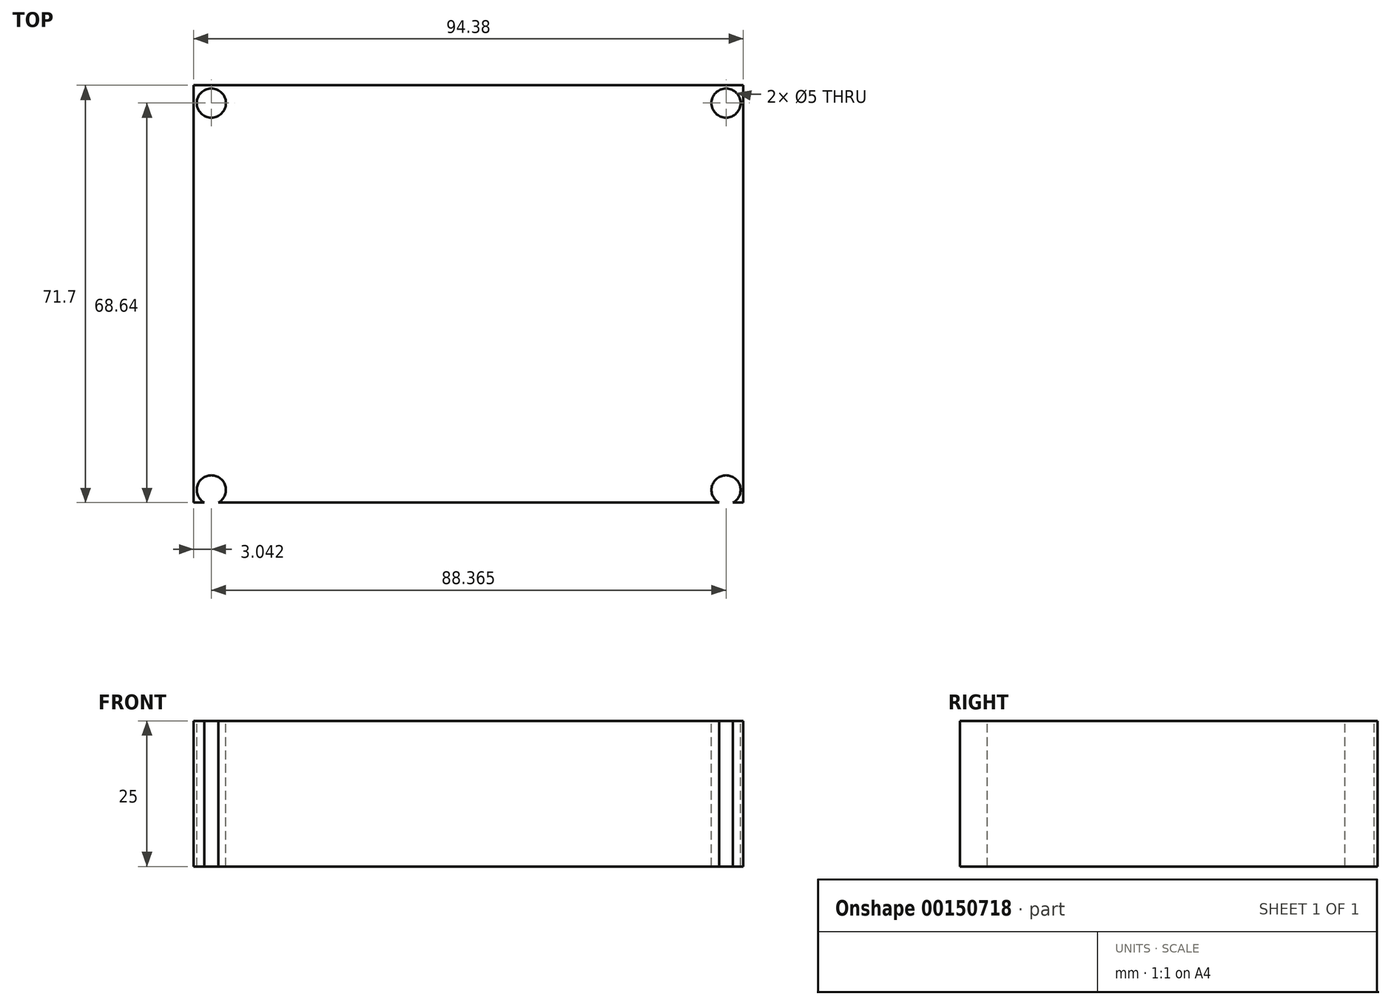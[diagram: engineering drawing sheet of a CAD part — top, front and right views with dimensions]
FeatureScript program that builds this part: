
annotation { "Feature Type Name" : "Feature", "Feature Type Description" : "" }
export const myFeature = defineFeature(function(context is Context, id is Id, definition is map)
    precondition{}
    {
        {
            var Q0;
            Q0=qCreatedBy(makeId("Top.planeOp"),FACE);
            var sketch = newSketch(context, id + "F0", { "sketchPlane" : qUnion([Q0])});
            skLineSegment(sketch, "E0.bottom", {"start": v(47.2, -35.85) * mm, "end": v(-47.2, -35.85) * mm});
            skLineSegment(sketch, "E0.top", {"start": v(47.2, 35.85) * mm, "end": v(-47.2, 35.85) * mm});
            skLineSegment(sketch, "E0.left", {"start": v(47.2, -35.85) * mm, "end": v(47.2, 35.85) * mm});
            skLineSegment(sketch, "E0.right", {"start": v(-47.2, -35.85) * mm, "end": v(-47.2, 35.85) * mm});
            skPoint(sketch, "E0.middle", {"position": v(0, 0) * mm});
            skSolve(sketch);
        }
        {
            var Q0;
            Q0=makeQuery(id+"F0.imprint","IMPRINT",FACE,{"disambiguationData":[TD([[makeQuery(id+"F0.imprint","IMPRINT",EDGE,{"derivedFrom":sQuery(id+"F0.wireOp",EDGE,"E0.bottom")}),-1.0]])]});
            extrude(context, id + "F1", {"entities" : qUnion([Q0]), "depth" : 25 * mm});
        }
        {
            var Q0;
            Q0=makeQuery(id+"F1.opExtrude","CAP_FACE",FACE,{"disambiguationData":[OSD([sQuery(id+"F0.wireOp",EDGE,"E0.bottom"),sQuery(id+"F0.wireOp",EDGE,"E0.top"),sQuery(id+"F0.wireOp",EDGE,"E0.left"),sQuery(id+"F0.wireOp",EDGE,"E0.right")])],"isStart":false});
            var sketch = newSketch(context, id + "F2", { "sketchPlane" : qUnion([Q0])});
            skPoint(sketch, "E1", {"position": v(-44.15, 32.8) * mm});
            skPoint(sketch, "E2", {"position": v(-44.15, -33.66) * mm});
            skPoint(sketch, "E3", {"position": v(44.22, -33.66) * mm});
            skPoint(sketch, "E4", {"position": v(44.22, 32.8) * mm});
            skSolve(sketch);
        }
        {
            var Q0;
            Q0=sQuery(id+"F2.wireOp",VERTEX,"E1");
            var Q1;
            Q1=sQuery(id+"F2.wireOp",VERTEX,"E2");
            var Q2;
            Q2=sQuery(id+"F2.wireOp",VERTEX,"E4");
            var Q3;
            Q3=sQuery(id+"F2.wireOp",VERTEX,"E3");
            var Q4;
            Q4=makeQuery(id+"F1.opExtrude","SWEPT_BODY",BODY,{"disambiguationData":[OSD([sQuery(id+"F0.wireOp",EDGE,"E0.bottom"),sQuery(id+"F0.wireOp",EDGE,"E0.top"),sQuery(id+"F0.wireOp",EDGE,"E0.left"),sQuery(id+"F0.wireOp",EDGE,"E0.right")])]});
            hole(context, id + "F3", {"style" : HoleStyle.SIMPLE, "endStyle" : HoleEndStyle.THROUGH, "holeDiameter" : 5 * mm, "locations" : qUnion([Q0, Q1, Q2, Q3]), "scope" : qUnion([Q4]), "isTappedThrough" : true});
        }
    });
